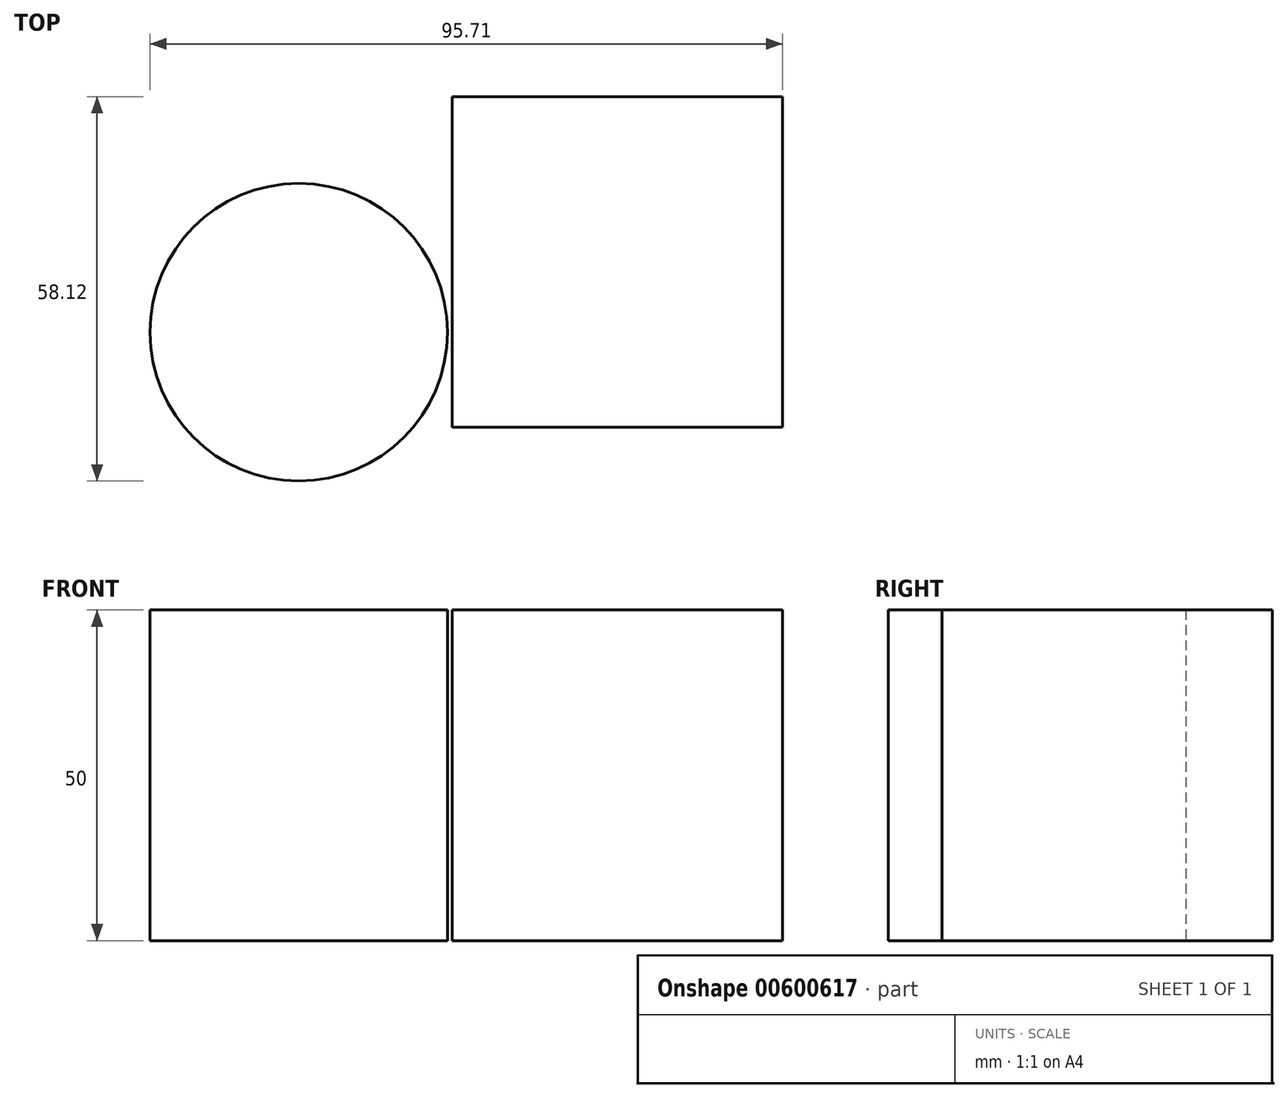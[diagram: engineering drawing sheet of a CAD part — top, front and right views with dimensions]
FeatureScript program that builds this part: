
annotation { "Feature Type Name" : "Feature", "Feature Type Description" : "" }
export const myFeature = defineFeature(function(context is Context, id is Id, definition is map)
    precondition{}
    {
        {
            var Q0;
            Q0=qCreatedBy(makeId("Top.planeOp"),FACE);
            var sketch = newSketch(context, id + "F0", { "sketchPlane" : qUnion([Q0])});
            skLineSegment(sketch, "E0.bottom", {"start": v(-25, -25) * mm, "end": v(25, -25) * mm});
            skLineSegment(sketch, "E0.top", {"start": v(-25, 25) * mm, "end": v(25, 25) * mm});
            skLineSegment(sketch, "E0.left", {"start": v(-25, -25) * mm, "end": v(-25, 25) * mm});
            skLineSegment(sketch, "E0.right", {"start": v(25, -25) * mm, "end": v(25, 25) * mm});
            skPoint(sketch, "E0.middle", {"position": v(0, 0) * mm});
            skCircle(sketch, "E1", {"center": v(-48.2, -10.62) * mm, "radius": 22.5 * mm});
            skArc(sketch, "E2", {"start": v(-33.55, -22.08) * mm, "mid": v(-48.48, 7.99) * mm, "end": v(-62.53, -22.5) * mm});
            skArc(sketch, "E3", {"start": v(-37.3, -20.2) * mm, "mid": v(-48.2, 3.9) * mm, "end": v(-59.12, -20.2) * mm});
            skSolve(sketch);
        }
        {
            var Q0;
            Q0 = qSketchRegion(id + "F0", true);
            extrude(context, id + "F1", {"entities" : qUnion([Q0]), "depth" : 50 * mm, "offsetDistance" : 25 * mm});
        }
    });
